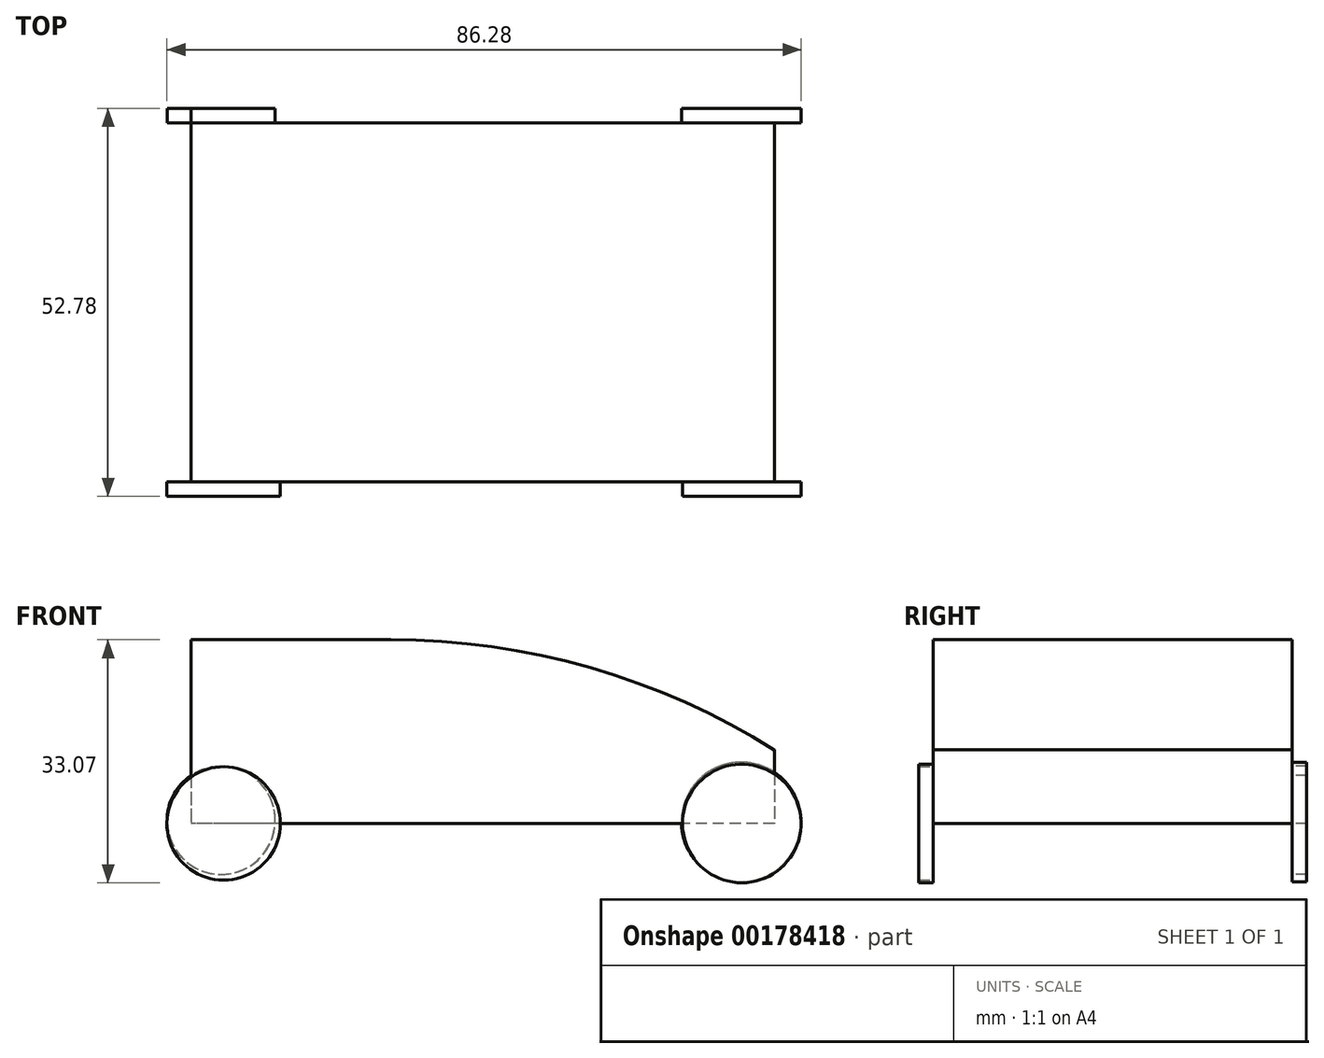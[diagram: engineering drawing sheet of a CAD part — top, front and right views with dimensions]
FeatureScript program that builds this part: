
annotation { "Feature Type Name" : "Feature", "Feature Type Description" : "" }
export const myFeature = defineFeature(function(context is Context, id is Id, definition is map)
    precondition{}
    {
        {
            var Q0;
            Q0=qCreatedBy(makeId("Top.planeOp"),FACE);
            var sketch = newSketch(context, id + "F0", { "sketchPlane" : qUnion([Q0])});
            skLineSegment(sketch, "E0.bottom", {"start": v(39.7, -24.4) * mm, "end": v(-39.7, -24.4) * mm});
            skLineSegment(sketch, "E0.top", {"start": v(39.7, 24.4) * mm, "end": v(-39.7, 24.4) * mm});
            skLineSegment(sketch, "E0.left", {"start": v(39.7, -24.4) * mm, "end": v(39.7, 24.4) * mm});
            skLineSegment(sketch, "E0.right", {"start": v(-39.7, -24.4) * mm, "end": v(-39.7, 24.4) * mm});
            skPoint(sketch, "E0.middle", {"position": v(0, 0) * mm});
            skSolve(sketch);
        }
        {
            var Q0;
            Q0=makeQuery(id+"F0.imprint","IMPRINT",FACE,{"disambiguationData":[TD([[makeQuery(id+"F0.imprint","IMPRINT",EDGE,{"derivedFrom":sQuery(id+"F0.wireOp",EDGE,"E0.bottom")}),-1.0]])]});
            extrude(context, id + "F1", {"entities" : qUnion([Q0]), "depth" : 20 * mm});
        }
        {
            var Q0;
            Q0=makeQuery(id+"F1.opExtrude","SWEPT_FACE",FACE,{"disambiguationData":[OSD([sQuery(id+"F0.wireOp",EDGE,"E0.bottom")])]});
            var sketch = newSketch(context, id + "F2", { "sketchPlane" : qUnion([Q0])});
            skCircle(sketch, "E1", {"center": v(-35.25, 0) * mm, "radius": 7.72 * mm});
            skCircle(sketch, "E2", {"center": v(35.25, 0) * mm, "radius": 8.07 * mm});
            skSolve(sketch);
        }
        {
            var Q0;
            {var subQ0=sQuery(id+"F2.wireOp",EDGE,"E1");var subQ1=sQuery(id+"F0.wireOp",EDGE,"E0.bottom");var subQ4=makeQuery(id+"F1.opExtrude","CAP_EDGE",EDGE,{"disambiguationData":[OSD([subQ1])],"isStart":true});var subQ5=makeQuery(id+"F2.imprint","INTERSECT",VERTEX,{"derivedFrom":[subQ4,subQ0]});Q0=makeQuery(id+"F2.imprint","IMPRINT",FACE,{"disambiguationData":[TD([[makeQuery(id+"F2.imprint","IMPRINT",EDGE,{"disambiguationData":[TD([[subQ5,1.0]])],"derivedFrom":subQ0}),1.0]])]});}
            var Q1;
            {var subQ0=sQuery(id+"F2.wireOp",EDGE,"E1");var subQ1=sQuery(id+"F0.wireOp",EDGE,"E0.bottom");var subQ4=makeQuery(id+"F1.opExtrude","CAP_EDGE",EDGE,{"disambiguationData":[OSD([subQ1])],"isStart":true});var subQ5=makeQuery(id+"F2.imprint","INTERSECT",VERTEX,{"derivedFrom":[subQ4,subQ0]});Q1=makeQuery(id+"F2.imprint","IMPRINT",FACE,{"disambiguationData":[TD([[makeQuery(id+"F2.imprint","IMPRINT",EDGE,{"disambiguationData":[TD([[subQ5,-1.0]])],"derivedFrom":subQ0}),1.0]])]});}
            extrude(context, id + "F3", {"entities" : qUnion([Q0, Q1]), "operationType" : NewBodyOperationType.ADD, "depth" : 2 * mm});
        }
        {
            var Q0;
            Q0 = qSketchRegion(id + "F2", true);
            extrude(context, id + "F4", {"entities" : qUnion([Q0]), "operationType" : NewBodyOperationType.ADD, "depth" : 2 * mm});
        }
        {
            var Q0;
            Q0=makeQuery(id+"F1.opExtrude","CAP_FACE",FACE,{"disambiguationData":[OSD([sQuery(id+"F0.wireOp",EDGE,"E0.bottom"),sQuery(id+"F0.wireOp",EDGE,"E0.top"),sQuery(id+"F0.wireOp",EDGE,"E0.left"),sQuery(id+"F0.wireOp",EDGE,"E0.right")])],"isStart":true});
            extrude(context, id + "F5", {"entities" : qUnion([Q0]), "operationType" : NewBodyOperationType.ADD, "oppositeDirection" : true, "depth" : 25 * mm});
        }
        {
            var Q0;
            {var subQ0=sQuery(id+"F0.wireOp",EDGE,"E0.top");Q0=makeQuery(id+"F5.boolean.opBoolean","MERGE",FACE,{"derivedFrom":[makeQuery(id+"F1.opExtrude","SWEPT_FACE",FACE,{"disambiguationData":[OSD([subQ0])]}),makeQuery(id+"F5.opExtrude","SWEPT_FACE",FACE,{"disambiguationData":[OSD([subQ0])]})]});}
            var sketch = newSketch(context, id + "F6", { "sketchPlane" : qUnion([Q0])});
            skCircle(sketch, "E3", {"center": v(-35.17, 0.2) * mm, "radius": 8.13 * mm});
            skPoint(sketch, "E3.first.point", {"position": v(-30.42, -6.4) * mm});
            skPoint(sketch, "E3.second.point", {"position": v(-39.7, 6.96) * mm});
            skPoint(sketch, "E3.third.point", {"position": v(-29.31, 5.84) * mm});
            skCircle(sketch, "E4", {"center": v(35.58, 0.43) * mm, "radius": 7.35 * mm});
            skPoint(sketch, "E4.first.point", {"position": v(39.7, -5.66) * mm});
            skPoint(sketch, "E4.second.point", {"position": v(30.6, 5.84) * mm});
            skPoint(sketch, "E4.third.point", {"position": v(42.11, 3.8) * mm});
            skSolve(sketch);
        }
        {
            var Q0;
            {var subQ0=sQuery(id+"F6.wireOp",EDGE,"E3");var subQ1=sQuery(id+"F0.wireOp",EDGE,"E0.top");var subQ2=makeQuery(id+"F1.opExtrude","CAP_EDGE",EDGE,{"disambiguationData":[OSD([subQ1])],"isStart":true});var subQ3=makeQuery(id+"F6.imprint","INTERSECT",VERTEX,{"derivedFrom":[subQ2,subQ0]});Q0=makeQuery(id+"F6.imprint","IMPRINT",FACE,{"disambiguationData":[TD([[makeQuery(id+"F6.imprint","IMPRINT",EDGE,{"disambiguationData":[TD([[subQ3,1.0]])],"derivedFrom":subQ0}),1.0]])]});}
            var Q1;
            {var subQ0=sQuery(id+"F6.wireOp",EDGE,"E3");var subQ1=sQuery(id+"F0.wireOp",EDGE,"E0.top");var subQ2=makeQuery(id+"F1.opExtrude","CAP_EDGE",EDGE,{"disambiguationData":[OSD([subQ1])],"isStart":true});var subQ3=makeQuery(id+"F6.imprint","INTERSECT",VERTEX,{"derivedFrom":[subQ2,subQ0]});Q1=makeQuery(id+"F6.imprint","IMPRINT",FACE,{"disambiguationData":[TD([[makeQuery(id+"F6.imprint","IMPRINT",EDGE,{"disambiguationData":[TD([[subQ3,-1.0]])],"derivedFrom":subQ0}),1.0]])]});}
            var Q2;
            {var subQ0=sQuery(id+"F6.wireOp",EDGE,"E4");var subQ1=sQuery(id+"F0.wireOp",EDGE,"E0.top");var subQ2=makeQuery(id+"F1.opExtrude","CAP_EDGE",EDGE,{"disambiguationData":[OSD([subQ1])],"isStart":true});var subQ3=makeQuery(id+"F6.imprint","INTERSECT",VERTEX,{"derivedFrom":[subQ2,subQ0]});Q2=makeQuery(id+"F6.imprint","IMPRINT",FACE,{"disambiguationData":[TD([[makeQuery(id+"F6.imprint","IMPRINT",EDGE,{"disambiguationData":[TD([[subQ3,-1.0]])],"derivedFrom":subQ0}),1.0]])]});}
            extrude(context, id + "F7", {"entities" : qUnion([Q0, Q1, Q2]), "operationType" : NewBodyOperationType.ADD, "depth" : 2 * mm});
        }
        {
            var Q0;
            Q0 = qSketchRegion(id + "F6", true);
            extrude(context, id + "F8", {"entities" : qUnion([Q0]), "depth" : 2 * mm});
        }
        {
            var Q0;
            Q0=makeQuery(id+"F5.opExtrude","CAP_EDGE",EDGE,{"disambiguationData":[OSD([sQuery(id+"F0.wireOp",EDGE,"E0.left")])],"isStart":false});
            chamfer(context, id + "F9", {"entities" : qUnion([Q0]), "width" : 15 * mm, "tangentPropagation" : true});
        }
        {
            var Q0;
            {var subQ0=sQuery(id+"F0.wireOp",EDGE,"E0.left");Q0=makeQuery(id+"F9.opChamfer","BLEND_EDGE",EDGE,{"blendedFrom":[makeQuery(id+"F5.opExtrude","CAP_EDGE",EDGE,{"disambiguationData":[OSD([subQ0])],"isStart":false}),makeQuery(id+"F5.opExtrude","CAP_FACE",FACE,{"disambiguationData":[OSD([sQuery(id+"F0.wireOp",EDGE,"E0.bottom"),sQuery(id+"F0.wireOp",EDGE,"E0.top"),subQ0,sQuery(id+"F0.wireOp",EDGE,"E0.right")])],"isStart":false})],"blendedInto":[makeQuery(id+"F5.opExtrude","CAP_FACE",FACE,{"disambiguationData":[OSD([sQuery(id+"F0.wireOp",EDGE,"E0.bottom"),sQuery(id+"F0.wireOp",EDGE,"E0.top"),subQ0,sQuery(id+"F0.wireOp",EDGE,"E0.right")])],"isStart":false})]});}
            fillet(context, id + "F10", {"entities" : qUnion([Q0]), "radius" : 98.31 * mm, "tangentPropagation" : true, "allowEdgeOverflow" : false});
        }
    });
